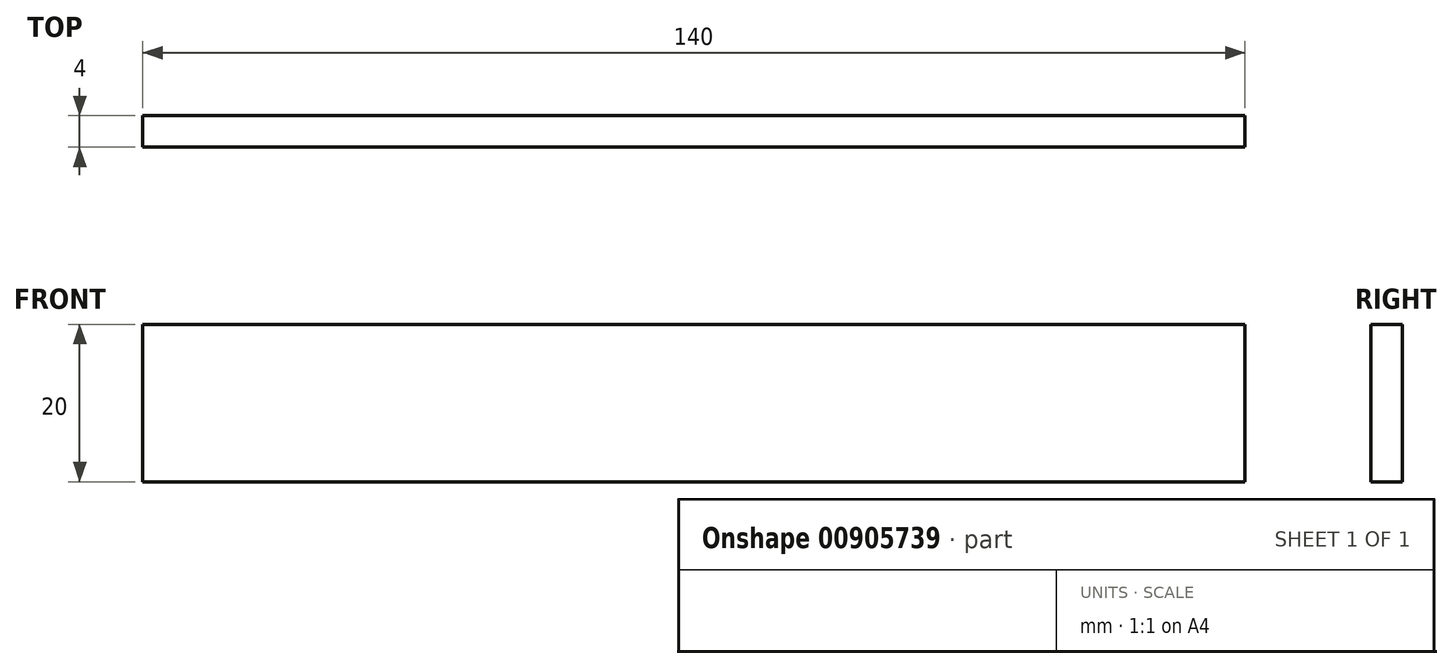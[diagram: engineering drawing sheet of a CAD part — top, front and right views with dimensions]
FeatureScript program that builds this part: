
annotation { "Feature Type Name" : "Feature", "Feature Type Description" : "" }
export const myFeature = defineFeature(function(context is Context, id is Id, definition is map)
    precondition{}
    {
        {
            var Q0;
            Q0=qCreatedBy(makeId("Front.planeOp"),FACE);
            var sketch = newSketch(context, id + "F0", { "sketchPlane" : qUnion([Q0])});
            skLineSegment(sketch, "E0.bottom", {"start": v(-57.41, -17.35) * mm, "end": v(82.59, -17.35) * mm});
            skLineSegment(sketch, "E0.top", {"start": v(-57.41, -37.35) * mm, "end": v(82.59, -37.35) * mm});
            skLineSegment(sketch, "E0.left", {"start": v(-57.41, -17.35) * mm, "end": v(-57.41, -37.35) * mm});
            skLineSegment(sketch, "E0.right", {"start": v(82.59, -17.35) * mm, "end": v(82.59, -37.35) * mm});
            skSolve(sketch);
        }
        {
            var Q0;
            Q0=makeQuery(id+"F0.imprint","IMPRINT",FACE,{"disambiguationData":[TD([[makeQuery(id+"F0.imprint","IMPRINT",EDGE,{"derivedFrom":sQuery(id+"F0.wireOp",EDGE,"E0.bottom")}),-1.0]])]});
            extrude(context, id + "F1", {"entities" : qUnion([Q0]), "depth" : 4 * mm, "offsetDistance" : 25 * mm});
        }
    });
